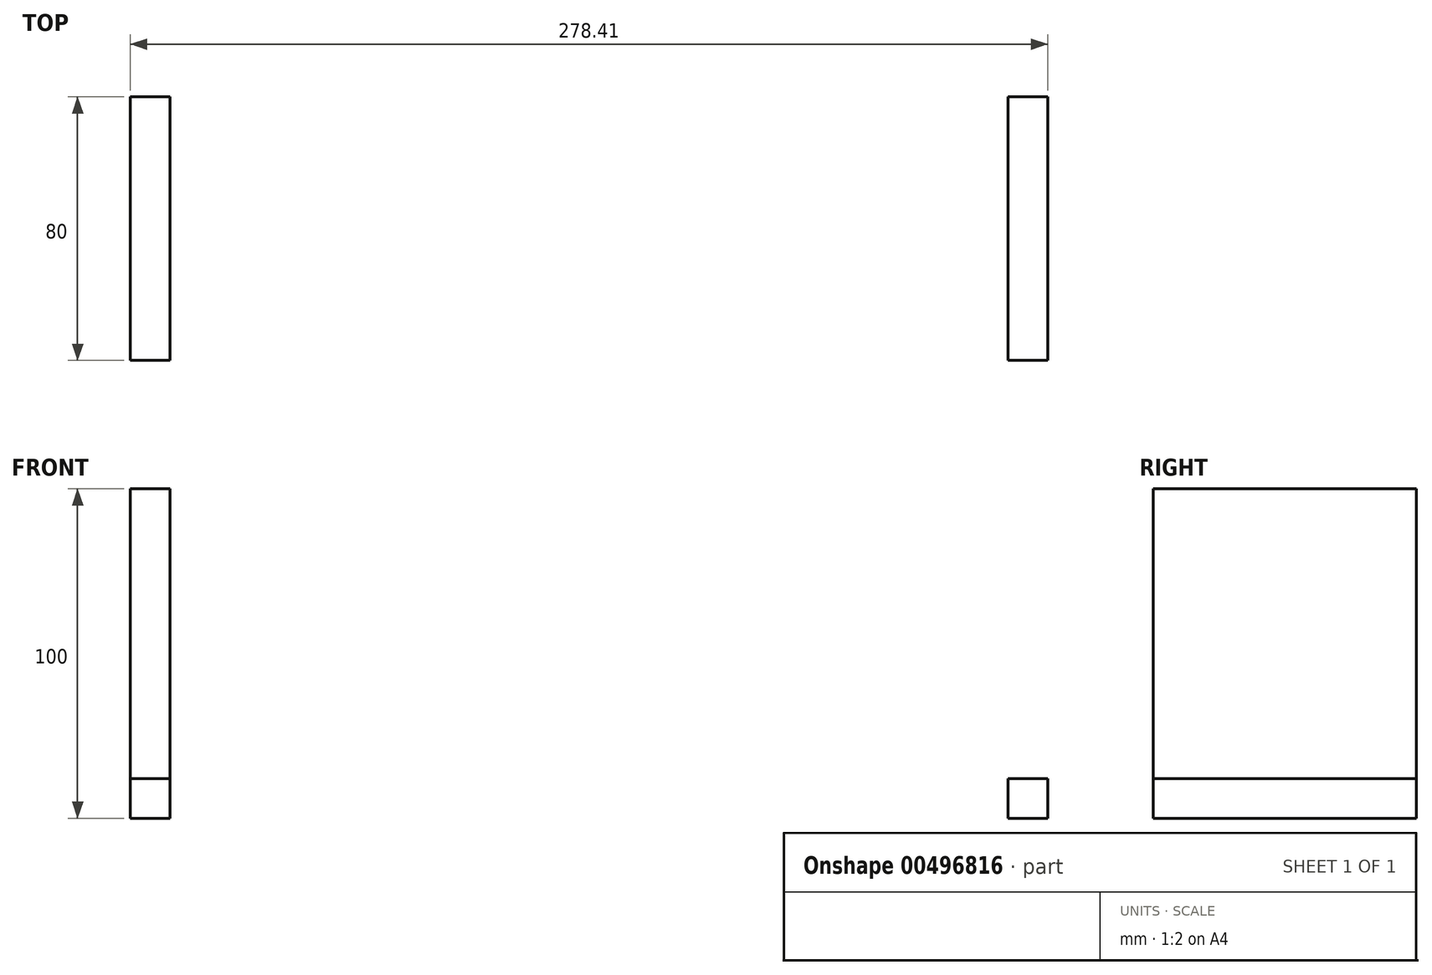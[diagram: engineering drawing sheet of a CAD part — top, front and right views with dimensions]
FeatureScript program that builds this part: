
annotation { "Feature Type Name" : "Feature", "Feature Type Description" : "" }
export const myFeature = defineFeature(function(context is Context, id is Id, definition is map)
    precondition{}
    {
        {
            var Q0;
            Q0=qCreatedBy(makeId("Top.planeOp"),FACE);
            var sketch = newSketch(context, id + "F0", { "sketchPlane" : qUnion([Q0])});
            skLineSegment(sketch, "E0.bottom", {"start": v(-55.48, 39.44) * mm, "end": v(-43.48, 39.44) * mm});
            skLineSegment(sketch, "E0.top", {"start": v(-55.48, -40.56) * mm, "end": v(-43.48, -40.56) * mm});
            skLineSegment(sketch, "E0.left", {"start": v(-55.48, 39.44) * mm, "end": v(-55.48, -40.56) * mm});
            skLineSegment(sketch, "E0.right", {"start": v(-43.48, 39.44) * mm, "end": v(-43.48, -40.56) * mm});
            skLineSegment(sketch, "E1.bottom", {"start": v(210.93, 39.44) * mm, "end": v(222.93, 39.44) * mm});
            skLineSegment(sketch, "E1.top", {"start": v(210.93, -40.56) * mm, "end": v(222.93, -40.56) * mm});
            skLineSegment(sketch, "E1.left", {"start": v(210.93, 39.44) * mm, "end": v(210.93, -40.56) * mm});
            skLineSegment(sketch, "E1.right", {"start": v(222.93, 39.44) * mm, "end": v(222.93, -40.56) * mm});
            skSolve(sketch);
        }
        {
            var Q0;
            Q0=makeQuery(id+"F0.imprint","IMPRINT",FACE,{"disambiguationData":[TD([[makeQuery(id+"F0.imprint","IMPRINT",EDGE,{"derivedFrom":sQuery(id+"F0.wireOp",EDGE,"E0.bottom")}),-1.0]])]});
            extrude(context, id + "F1", {"entities" : qUnion([Q0]), "depth" : 100 * mm});
        }
        {
            var Q0;
            Q0 = qSketchRegion(id + "F0", true);
            extrude(context, id + "F2", {"entities" : qUnion([Q0]), "operationType" : NewBodyOperationType.ADD, "depth" : 12 * mm});
        }
        {
            var Q0;
            Q0 = qSketchRegion(id + "F0", true);
            var Q1;
            Q1 = qSketchRegion(id + "F8GmjscwmfdzMq0_3", true);
            extrude(context, id + "F3", {"entities" : qUnion([Q0, Q1]), "depth" : 12 * mm});
        }
    });
